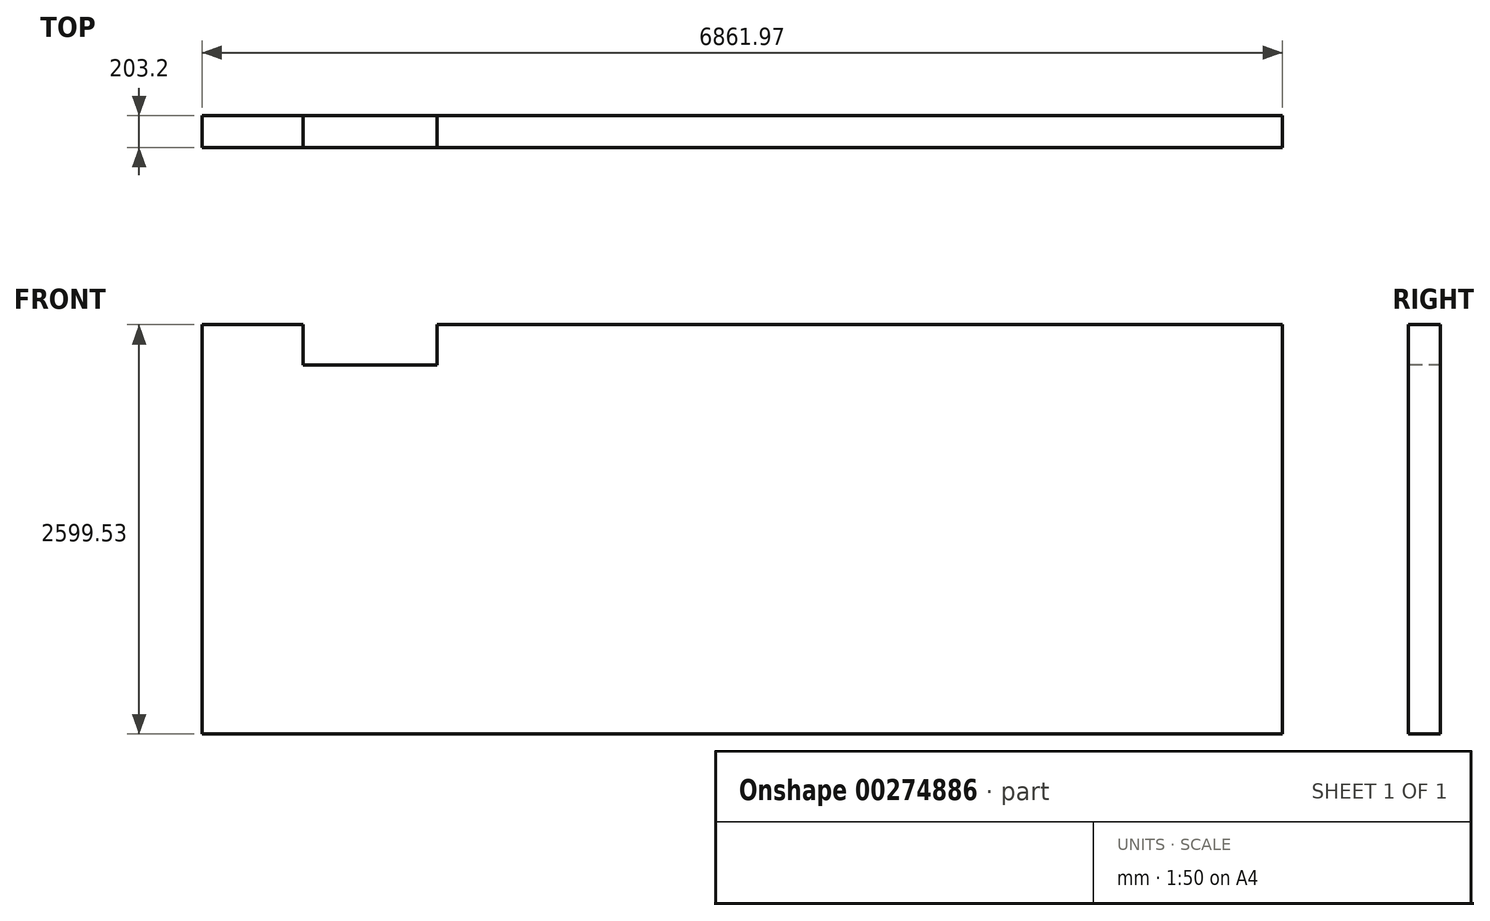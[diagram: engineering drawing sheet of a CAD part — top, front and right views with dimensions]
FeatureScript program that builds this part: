
annotation { "Feature Type Name" : "Feature", "Feature Type Description" : "" }
export const myFeature = defineFeature(function(context is Context, id is Id, definition is map)
    precondition{}
    {
        {
            var Q0;
            Q0=qCreatedBy(makeId("Top.planeOp"),FACE);
            var sketch = newSketch(context, id + "F0", { "sketchPlane" : qUnion([Q0])});
            skLineSegment(sketch, "E0.bottom", {"start": v(0, 0) * mm, "end": v(7268.37, 0) * mm});
            skLineSegment(sketch, "E0.top", {"start": v(0, 4074.32) * mm, "end": v(7268.37, 4074.32) * mm});
            skLineSegment(sketch, "E0.left", {"start": v(0, 0) * mm, "end": v(0, 4074.32) * mm});
            skLineSegment(sketch, "E0.right", {"start": v(7268.37, 0) * mm, "end": v(7268.37, 4074.32) * mm});
            skLineSegment(sketch, "E1.bottom", {"start": v(0, 0) * mm, "end": v(203.2, 0) * mm, "construction": true});
            skLineSegment(sketch, "E1.top", {"start": v(0, 203.2) * mm, "end": v(203.2, 203.2) * mm, "construction": true});
            skLineSegment(sketch, "E1.left", {"start": v(0, 0) * mm, "end": v(0, 203.2) * mm, "construction": true});
            skLineSegment(sketch, "E1.right", {"start": v(203.2, 0) * mm, "end": v(203.2, 203.2) * mm, "construction": true});
            skLineSegment(sketch, "E2.bottom", {"start": v(7268.37, 0) * mm, "end": v(7065.17, 0) * mm, "construction": true});
            skLineSegment(sketch, "E2.top", {"start": v(7268.37, 203.2) * mm, "end": v(7065.17, 203.2) * mm, "construction": true});
            skLineSegment(sketch, "E2.left", {"start": v(7268.37, 0) * mm, "end": v(7268.37, 203.2) * mm, "construction": true});
            skLineSegment(sketch, "E2.right", {"start": v(7065.17, 0) * mm, "end": v(7065.17, 203.2) * mm, "construction": true});
            skLineSegment(sketch, "E3.bottom", {"start": v(7268.37, 4074.32) * mm, "end": v(7065.17, 4074.32) * mm, "construction": true});
            skLineSegment(sketch, "E3.top", {"start": v(7268.37, 3871.12) * mm, "end": v(7065.17, 3871.12) * mm, "construction": true});
            skLineSegment(sketch, "E3.left", {"start": v(7268.37, 4074.32) * mm, "end": v(7268.37, 3871.12) * mm, "construction": true});
            skLineSegment(sketch, "E3.right", {"start": v(7065.17, 4074.32) * mm, "end": v(7065.17, 3871.12) * mm, "construction": true});
            skLineSegment(sketch, "E4.bottom", {"start": v(0, 4074.32) * mm, "end": v(203.2, 4074.32) * mm, "construction": true});
            skLineSegment(sketch, "E4.top", {"start": v(0, 3871.12) * mm, "end": v(203.2, 3871.12) * mm, "construction": true});
            skLineSegment(sketch, "E4.left", {"start": v(0, 4074.32) * mm, "end": v(0, 3871.12) * mm, "construction": true});
            skLineSegment(sketch, "E4.right", {"start": v(203.2, 4074.32) * mm, "end": v(203.2, 3871.12) * mm, "construction": true});
            skLineSegment(sketch, "E5.bottom", {"start": v(203.2, 3871.12) * mm, "end": v(7065.17, 3871.12) * mm});
            skLineSegment(sketch, "E5.top", {"start": v(203.2, 203.2) * mm, "end": v(7065.17, 203.2) * mm});
            skLineSegment(sketch, "E5.left", {"start": v(203.2, 3871.12) * mm, "end": v(203.2, 203.2) * mm});
            skLineSegment(sketch, "E5.right", {"start": v(7065.17, 3871.12) * mm, "end": v(7065.17, 203.2) * mm});
            skSolve(sketch);
        }
        {
            var Q0;
            Q0=makeQuery(id+"F0.imprint","IMPRINT",FACE,{"disambiguationData":[TD([[makeQuery(id+"F0.imprint","IMPRINT",EDGE,{"derivedFrom":sQuery(id+"F0.wireOp",EDGE,"E0.bottom")}),1.0]])]});
            extrude(context, id + "F1", {"entities" : qUnion([Q0]), "depth" : 2599.53 * mm});
        }
        {
            var Q0;
            Q0=qCreatedBy(makeId("Front.planeOp"),FACE);
            var sketch = newSketch(context, id + "F2", { "sketchPlane" : qUnion([Q0])});
            skLineSegment(sketch, "E6.bottom", {"start": v(0, 0) * mm, "end": v(1263.65, 0) * mm, "construction": true});
            skLineSegment(sketch, "E6.top", {"start": v(0, 2342.36) * mm, "end": v(1263.65, 2342.36) * mm, "construction": true});
            skLineSegment(sketch, "E6.left", {"start": v(0, 0) * mm, "end": v(0, 2342.36) * mm, "construction": true});
            skLineSegment(sketch, "E6.right", {"start": v(1263.65, 0) * mm, "end": v(1263.65, 2342.36) * mm, "construction": true});
            skLineSegment(sketch, "E7.bottom", {"start": v(1263.65, 2342.36) * mm, "end": v(1695.45, 2342.36) * mm});
            skLineSegment(sketch, "E7.top", {"start": v(1263.65, 2475.7) * mm, "end": v(1695.45, 2475.7) * mm});
            skLineSegment(sketch, "E7.left", {"start": v(1263.65, 2342.36) * mm, "end": v(1263.65, 2475.7) * mm});
            skLineSegment(sketch, "E7.right", {"start": v(1695.45, 2342.36) * mm, "end": v(1695.45, 2475.7) * mm});
            skSolve(sketch);
        }
        {
            var Q0;
            Q0=makeQuery(id+"F2.imprint","IMPRINT",FACE,{"disambiguationData":[TD([[makeQuery(id+"F2.imprint","IMPRINT",EDGE,{"derivedFrom":sQuery(id+"F2.wireOp",EDGE,"E7.bottom")}),1.0]])]});
            extrude(context, id + "F3", {"entities" : qUnion([Q0]), "operationType" : NewBodyOperationType.REMOVE, "oppositeDirection" : true, "depth" : 203.2 * mm});
        }
        {
            var Q0;
            Q0=makeQuery(id+"F1.opExtrude","SWEPT_FACE",FACE,{"disambiguationData":[OSD([sQuery(id+"F0.wireOp",EDGE,"E5.top")])]});
            var sketch = newSketch(context, id + "F4", { "sketchPlane" : qUnion([Q0])});
            skLineSegment(sketch, "E8.bottom", {"start": v(-7065.17, 0) * mm, "end": v(-6230.15, 0) * mm, "construction": true});
            skLineSegment(sketch, "E8.top", {"start": v(-7065.17, 2235.2) * mm, "end": v(-6230.15, 2235.2) * mm, "construction": true});
            skLineSegment(sketch, "E8.left", {"start": v(-7065.17, 0) * mm, "end": v(-7065.17, 2235.2) * mm, "construction": true});
            skLineSegment(sketch, "E8.right", {"start": v(-6230.15, 0) * mm, "end": v(-6230.15, 2235.2) * mm, "construction": true});
            skLineSegment(sketch, "E9.bottom", {"start": v(-6230.15, 2235.2) * mm, "end": v(-5925.35, 2235.2) * mm});
            skLineSegment(sketch, "E9.top", {"start": v(-6230.15, 2489.2) * mm, "end": v(-5925.35, 2489.2) * mm});
            skLineSegment(sketch, "E9.left", {"start": v(-6230.15, 2235.2) * mm, "end": v(-6230.15, 2489.2) * mm});
            skLineSegment(sketch, "E9.right", {"start": v(-5925.35, 2235.2) * mm, "end": v(-5925.35, 2489.2) * mm});
            skSolve(sketch);
        }
        {
            var Q0;
            Q0=makeQuery(id+"F4.imprint","IMPRINT",FACE,{"disambiguationData":[TD([[makeQuery(id+"F4.imprint","IMPRINT",EDGE,{"derivedFrom":sQuery(id+"F4.wireOp",EDGE,"E9.bottom")}),1.0]])]});
            extrude(context, id + "F5", {"entities" : qUnion([Q0]), "operationType" : NewBodyOperationType.REMOVE, "oppositeDirection" : true, "depth" : 203.2 * mm});
        }
        {
            var Q0;
            Q0=makeQuery(id+"F3.boolean.opBoolean","COPY",FACE,{"derivedFrom":makeQuery(id+"F3.opExtrude","SWEPT_FACE",FACE,{"disambiguationData":[OSD([sQuery(id+"F2.wireOp",EDGE,"E7.left")])]})});
            extrude(context, id + "F6", {"entities" : qUnion([Q0]), "operationType" : NewBodyOperationType.REMOVE, "oppositeDirection" : true, "depth" : 381 * mm});
        }
        {
            var Q0;
            Q0=makeQuery(id+"F5.boolean.opBoolean","COPY",FACE,{"derivedFrom":makeQuery(id+"F5.opExtrude","SWEPT_FACE",FACE,{"disambiguationData":[OSD([sQuery(id+"F4.wireOp",EDGE,"E9.bottom")])]})});
            var Q1;
            Q1=makeQuery(id+"F5.boolean.opBoolean","COPY",FACE,{"derivedFrom":makeQuery(id+"F5.opExtrude","SWEPT_FACE",FACE,{"disambiguationData":[OSD([sQuery(id+"F4.wireOp",EDGE,"E9.top")])]})});
            extrude(context, id + "F7", {"entities" : qUnion([Q0]), "operationType" : NewBodyOperationType.ADD, "endBound" : BoundingType.UP_TO_SURFACE, "endBoundEntityFace" : qUnion([Q1]), "depth" : 25.4 * mm});
        }
        {
            var Q0;
            {var subQ0=sQuery(id+"F2.wireOp",EDGE,"E7.top");Q0=makeQuery(id+"F6.boolean.opBoolean","MERGE",FACE,{"derivedFrom":[makeQuery(id+"F3.boolean.opBoolean","COPY",FACE,{"derivedFrom":makeQuery(id+"F3.opExtrude","SWEPT_FACE",FACE,{"disambiguationData":[OSD([subQ0])]})}),makeQuery(id+"F6.opExtrude","SWEPT_FACE",FACE,{"disambiguationData":[OSD([subQ0,sQuery(id+"F2.wireOp",EDGE,"E7.left")])]})]});}
            extrude(context, id + "F8", {"entities" : qUnion([Q0]), "operationType" : NewBodyOperationType.REMOVE, "oppositeDirection" : true, "depth" : 106.68 * mm});
        }
        {
            var Q0;
            {var subQ0=sQuery(id+"F2.wireOp",EDGE,"E7.left");var subQ1=sQuery(id+"F2.wireOp",EDGE,"E7.top");Q0=makeQuery(id+"F8.boolean.opBoolean","MERGE",FACE,{"derivedFrom":[makeQuery(id+"F6.boolean.opBoolean","COPY",FACE,{"derivedFrom":makeQuery(id+"F6.opExtrude","CAP_FACE",FACE,{"disambiguationData":[OSD([subQ0])],"isStart":false})}),makeQuery(id+"F8.opExtrude","SWEPT_FACE",FACE,{"disambiguationData":[OSD([subQ1,subQ0]),TDD([makeQuery(id+"F6.boolean.opBoolean","COPY",EDGE,{"derivedFrom":makeQuery(id+"F6.opExtrude","CAP_EDGE",EDGE,{"disambiguationData":[OSD([subQ1,subQ0])],"isStart":false})})])]})]});}
            extrude(context, id + "F9", {"entities" : qUnion([Q0]), "operationType" : NewBodyOperationType.REMOVE, "oppositeDirection" : true, "depth" : 38.1 * mm});
        }
        {
            var Q0;
            {var subQ0=sQuery(id+"F2.wireOp",EDGE,"E7.left");var subQ1=sQuery(id+"F2.wireOp",EDGE,"E7.top");Q0=makeQuery(id+"F9.boolean.opBoolean","MERGE",FACE,{"derivedFrom":[makeQuery(id+"F8.boolean.opBoolean","COPY",FACE,{"derivedFrom":makeQuery(id+"F8.opExtrude","CAP_FACE",FACE,{"disambiguationData":[OSD([subQ1,subQ0])],"isStart":false})}),makeQuery(id+"F9.opExtrude","SWEPT_FACE",FACE,{"disambiguationData":[OSD([subQ1,subQ0]),TDD([makeQuery(id+"F8.boolean.opBoolean","COPY",EDGE,{"derivedFrom":makeQuery(id+"F8.opExtrude","CAP_EDGE",EDGE,{"disambiguationData":[OSD([subQ1,subQ0]),TDD([makeQuery(id+"F6.boolean.opBoolean","COPY",EDGE,{"derivedFrom":makeQuery(id+"F6.opExtrude","CAP_EDGE",EDGE,{"disambiguationData":[OSD([subQ1,subQ0])],"isStart":false})})])],"isStart":false})})])]})]});}
            var Q1;
            Q1=makeQuery(id+"F1.opExtrude","CAP_FACE",FACE,{"disambiguationData":[OSD([sQuery(id+"F0.wireOp",EDGE,"E0.bottom"),sQuery(id+"F0.wireOp",EDGE,"E0.top"),sQuery(id+"F0.wireOp",EDGE,"E0.left"),sQuery(id+"F0.wireOp",EDGE,"E0.right"),sQuery(id+"F0.wireOp",EDGE,"E5.bottom"),sQuery(id+"F0.wireOp",EDGE,"E5.top"),sQuery(id+"F0.wireOp",EDGE,"E5.left"),sQuery(id+"F0.wireOp",EDGE,"E5.right")])],"isStart":false});
            extrude(context, id + "F10", {"entities" : qUnion([Q0]), "operationType" : NewBodyOperationType.REMOVE, "endBound" : BoundingType.UP_TO_SURFACE, "oppositeDirection" : true, "endBoundEntityFace" : qUnion([Q1]), "depth" : 25.4 * mm});
        }
        {
            var Q0;
            Q0=makeQuery(id+"F1.opExtrude","SWEPT_FACE",FACE,{"disambiguationData":[OSD([sQuery(id+"F0.wireOp",EDGE,"E0.top")])]});
            var Q1;
            {var subQ0=sQuery(id+"F4.wireOp",EDGE,"E9.bottom");Q1=makeQuery(id+"F7.boolean.opBoolean","MERGE",FACE,{"derivedFrom":[makeQuery(id+"F1.opExtrude","SWEPT_FACE",FACE,{"disambiguationData":[OSD([sQuery(id+"F0.wireOp",EDGE,"E5.top")])]}),makeQuery(id+"F7.opExtrude","SWEPT_FACE",FACE,{"disambiguationData":[OSD([subQ0]),TDD([makeQuery(id+"F5.boolean.opBoolean","COPY",EDGE,{"derivedFrom":makeQuery(id+"F5.opExtrude","CAP_EDGE",EDGE,{"disambiguationData":[OSD([subQ0])],"isStart":true})})])]})]});}
            extrude(context, id + "F11", {"entities" : qUnion([Q0]), "operationType" : NewBodyOperationType.REMOVE, "endBound" : BoundingType.UP_TO_SURFACE, "oppositeDirection" : true, "endBoundEntityFace" : qUnion([Q1]), "depth" : 25.4 * mm});
        }
        {
            var Q0;
            Q0=makeQuery(id+"F1.opExtrude","SWEPT_FACE",FACE,{"disambiguationData":[OSD([sQuery(id+"F0.wireOp",EDGE,"E0.right")])]});
            extrude(context, id + "F12", {"entities" : qUnion([Q0]), "operationType" : NewBodyOperationType.REMOVE, "oppositeDirection" : true, "depth" : 203.2 * mm});
        }
        {
            var Q0;
            Q0=makeQuery(id+"F1.opExtrude","SWEPT_FACE",FACE,{"disambiguationData":[OSD([sQuery(id+"F0.wireOp",EDGE,"E0.left")])]});
            extrude(context, id + "F13", {"entities" : qUnion([Q0]), "operationType" : NewBodyOperationType.REMOVE, "oppositeDirection" : true, "depth" : 203.2 * mm});
        }
    });
